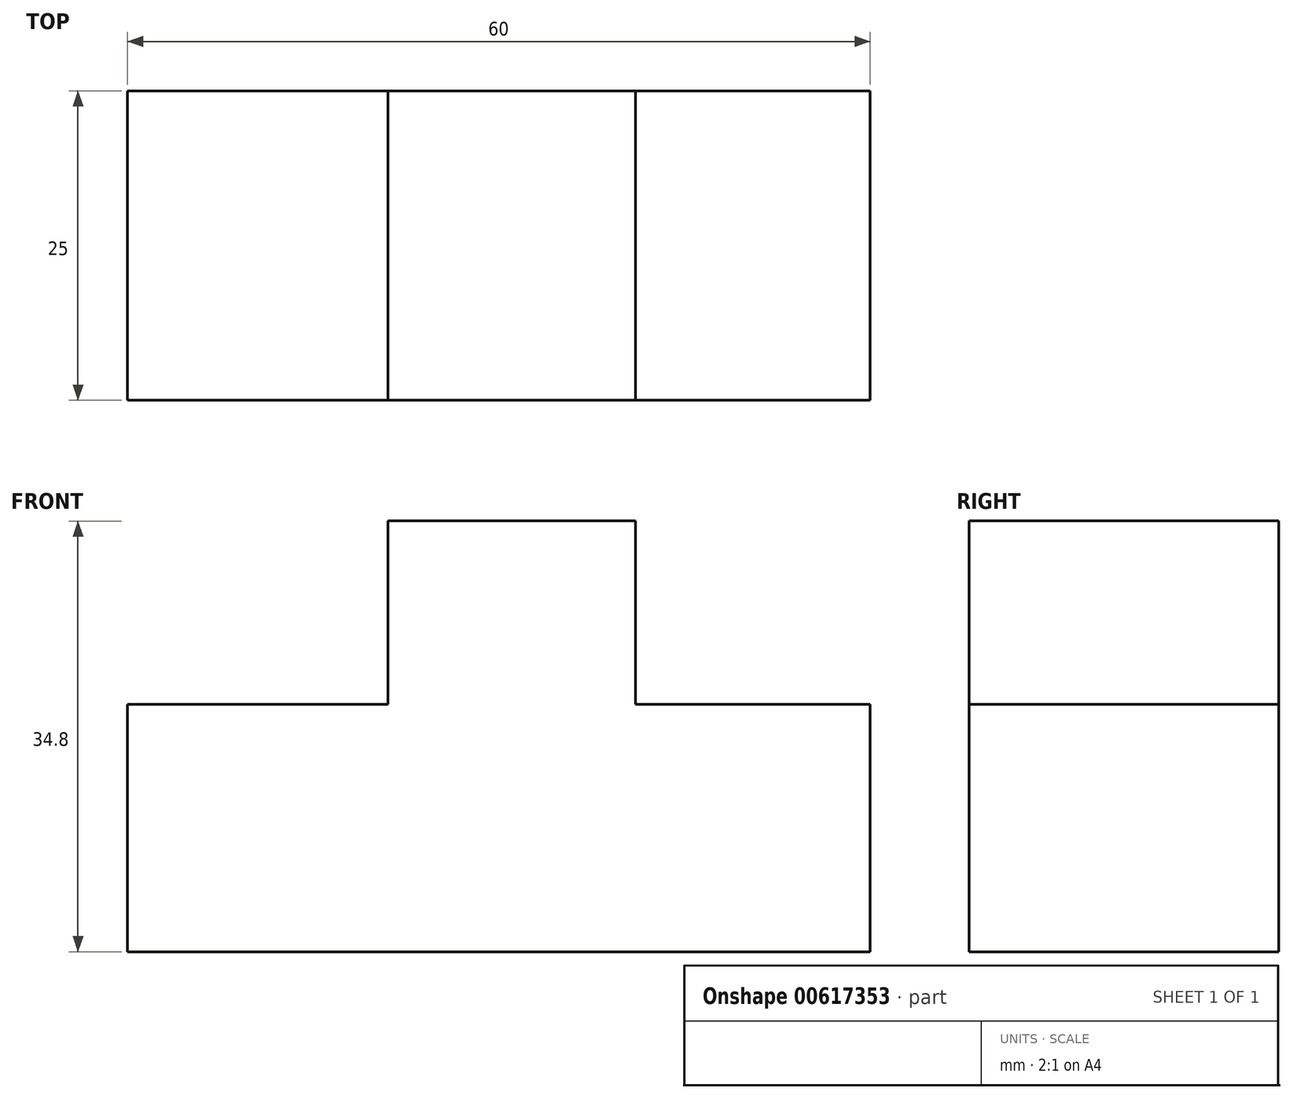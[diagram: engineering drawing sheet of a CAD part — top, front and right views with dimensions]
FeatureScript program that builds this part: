
annotation { "Feature Type Name" : "Feature", "Feature Type Description" : "" }
export const myFeature = defineFeature(function(context is Context, id is Id, definition is map)
    precondition{}
    {
        {
            var Q0;
            Q0=qCreatedBy(makeId("Front.planeOp"),FACE);
            var sketch = newSketch(context, id + "F0", { "sketchPlane" : qUnion([Q0])});
            skLineSegment(sketch, "E0", {"start": v(-25.06, -38.9) * mm, "end": v(34.94, -38.9) * mm});
            skLineSegment(sketch, "E1", {"start": v(34.94, -38.9) * mm, "end": v(34.94, -18.9) * mm});
            skLineSegment(sketch, "E2", {"start": v(34.94, -18.9) * mm, "end": v(-25.06, -18.9) * mm});
            skLineSegment(sketch, "E3", {"start": v(-25.06, -18.9) * mm, "end": v(-25.06, -38.9) * mm});
            skLineSegment(sketch, "E4", {"start": v(15.98, -18.9) * mm, "end": v(15.98, -4.1) * mm});
            skLineSegment(sketch, "E5", {"start": v(15.98, -4.1) * mm, "end": v(-4.02, -4.1) * mm});
            skLineSegment(sketch, "E6", {"start": v(-4.02, -4.1) * mm, "end": v(-4.02, -18.9) * mm});
            skSolve(sketch);
        }
        {
            var Q0;
            Q0 = qSketchRegion(id + "F0", true);
            extrude(context, id + "F1", {"entities" : qUnion([Q0]), "depth" : 25 * mm, "offsetDistance" : 25 * mm});
        }
    });
